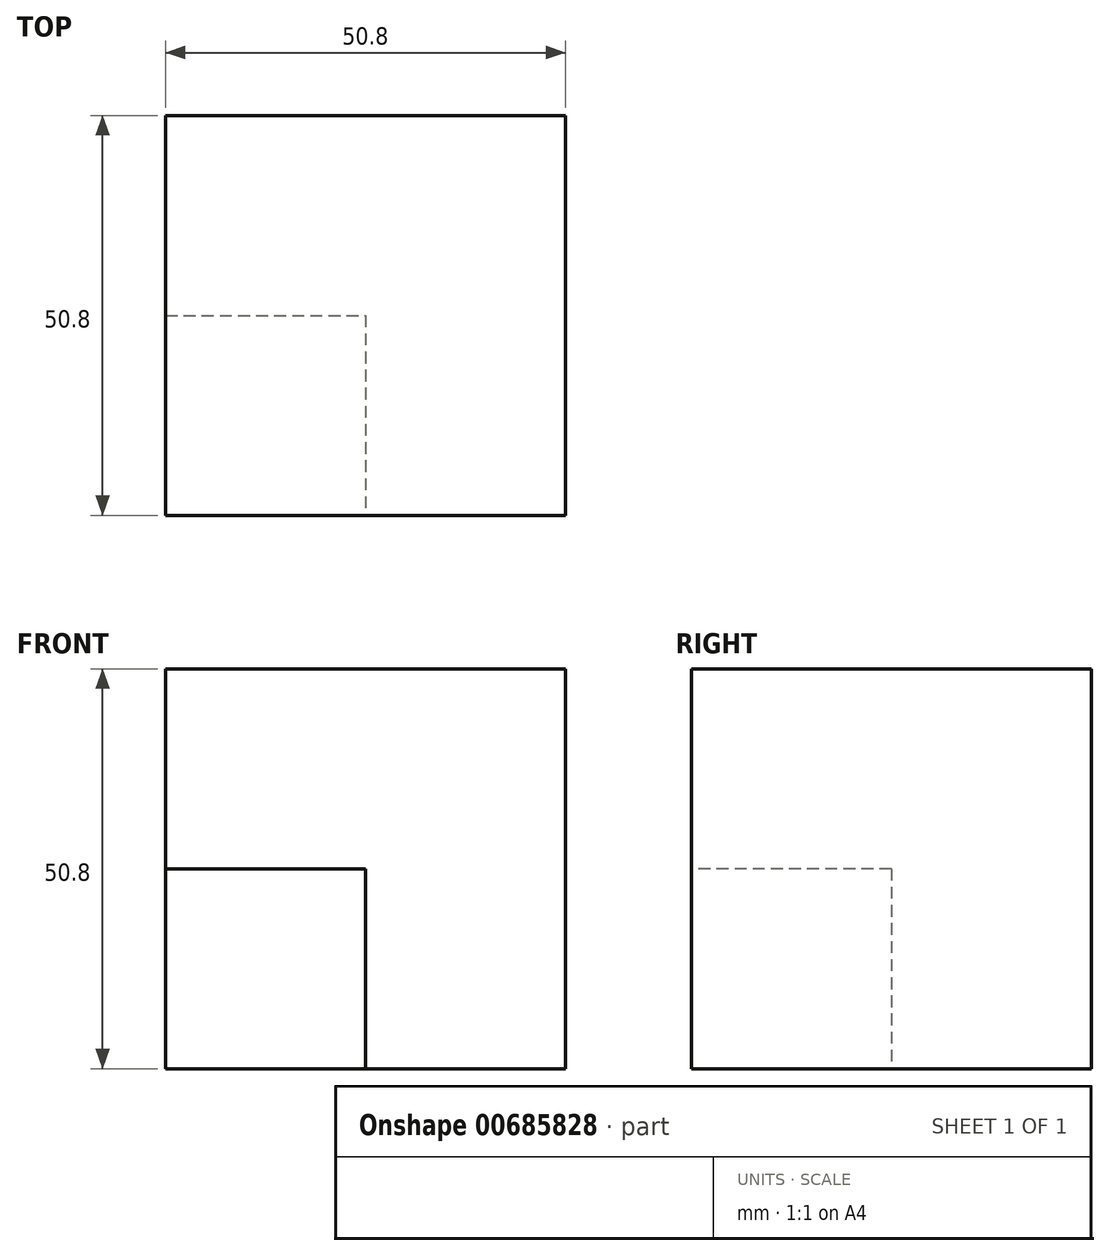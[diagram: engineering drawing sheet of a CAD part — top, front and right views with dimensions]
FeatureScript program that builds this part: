
annotation { "Feature Type Name" : "Feature", "Feature Type Description" : "" }
export const myFeature = defineFeature(function(context is Context, id is Id, definition is map)
    precondition{}
    {
        {
            var Q0;
            Q0=qCreatedBy(makeId("Front.planeOp"),FACE);
            var sketch = newSketch(context, id + "F0", { "sketchPlane" : qUnion([Q0])});
            skLineSegment(sketch, "E0.bottom", {"start": v(-27.98, 33.7) * mm, "end": v(22.82, 33.7) * mm});
            skLineSegment(sketch, "E0.top", {"start": v(-27.98, -17.1) * mm, "end": v(22.82, -17.1) * mm});
            skLineSegment(sketch, "E0.left", {"start": v(-27.98, 33.7) * mm, "end": v(-27.98, -17.1) * mm});
            skLineSegment(sketch, "E0.right", {"start": v(22.82, 33.7) * mm, "end": v(22.82, -17.1) * mm});
            skSolve(sketch);
        }
        {
            var Q0;
            Q0=makeQuery(id+"F0.imprint","IMPRINT",FACE,{"disambiguationData":[TD([[makeQuery(id+"F0.imprint","IMPRINT",EDGE,{"derivedFrom":sQuery(id+"F0.wireOp",EDGE,"E0.bottom")}),-1.0]])]});
            extrude(context, id + "F1", {"entities" : qUnion([Q0]), "depth" : 50.8 * mm, "offsetDistance" : 25.4 * mm});
        }
        {
            var Q0;
            Q0=makeQuery(id+"F1.opExtrude","CAP_FACE",FACE,{"disambiguationData":[OSD([sQuery(id+"F0.wireOp",EDGE,"E0.bottom"),sQuery(id+"F0.wireOp",EDGE,"E0.top"),sQuery(id+"F0.wireOp",EDGE,"E0.left"),sQuery(id+"F0.wireOp",EDGE,"E0.right")])],"isStart":false});
            var sketch = newSketch(context, id + "F2", { "sketchPlane" : qUnion([Q0])});
            skLineSegment(sketch, "E1.bottom", {"start": v(-27.98, -17.1) * mm, "end": v(-2.58, -17.1) * mm});
            skLineSegment(sketch, "E1.top", {"start": v(-27.98, 8.3) * mm, "end": v(-2.58, 8.3) * mm});
            skLineSegment(sketch, "E1.left", {"start": v(-27.98, -17.1) * mm, "end": v(-27.98, 8.3) * mm});
            skLineSegment(sketch, "E1.right", {"start": v(-2.58, -17.1) * mm, "end": v(-2.58, 8.3) * mm});
            skSolve(sketch);
        }
        {
            var Q0;
            Q0=makeQuery(id+"F2.imprint","IMPRINT",FACE,{"disambiguationData":[TD([[makeQuery(id+"F2.imprint","IMPRINT",EDGE,{"derivedFrom":sQuery(id+"F2.wireOp",EDGE,"E1.bottom")}),1.0]])]});
            extrude(context, id + "F3", {"entities" : qUnion([Q0]), "operationType" : NewBodyOperationType.REMOVE, "depth" : 25.4 * mm, "offsetDistance" : 25.4 * mm});
        }
        {
            var Q0;
            Q0=makeQuery(id+"F2.imprint","IMPRINT",FACE,{"disambiguationData":[TD([[makeQuery(id+"F2.imprint","IMPRINT",EDGE,{"derivedFrom":sQuery(id+"F2.wireOp",EDGE,"E1.bottom")}),1.0]])]});
            extrude(context, id + "F4", {"entities" : qUnion([Q0]), "operationType" : NewBodyOperationType.REMOVE, "oppositeDirection" : true, "depth" : 25.4 * mm, "offsetDistance" : 25.4 * mm});
        }
    });
